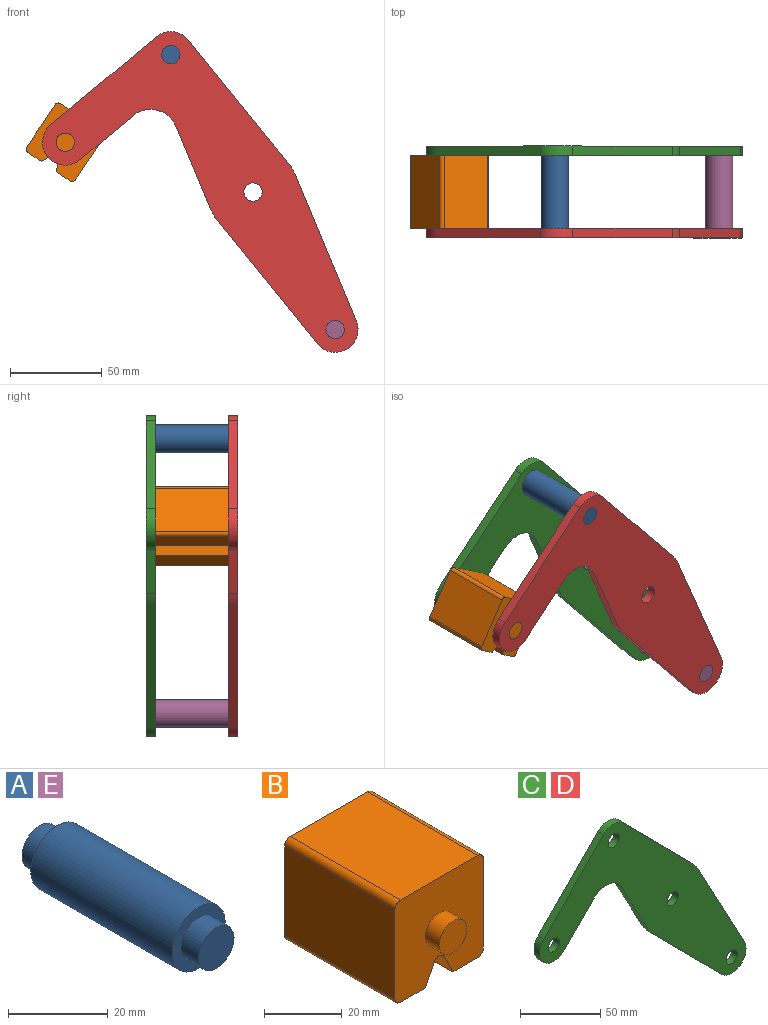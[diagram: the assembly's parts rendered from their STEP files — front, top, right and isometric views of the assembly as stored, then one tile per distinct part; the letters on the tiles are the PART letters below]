
ASSEMBLY  parts=5 mates=4
PART A: 7 faces, bbox 15x50x15 mm
  f0: cylinder r=7.5mm len=40mm, axis (0,-1,0), area 1885mm2, adj f2,f5
  f1: cylinder r=5mm len=10mm, axis (0,1,0), area 157.1mm2, adj f2,f3
  f2: plane 15x15mm, normal (0,-1,0), area 98.2mm2, adj f0,f1
  f3: plane 10x10mm, normal (0,-1,0), area 78.5mm2, adj f1
  f4: cylinder r=5mm len=10mm, axis (0,-1,0), area 157.1mm2, adj f5,f6
  f5: plane 15x15mm, normal (0,1,0), area 98.2mm2, adj f0,f4
  f6: plane 10x10mm, normal (0,1,0), area 78.5mm2, adj f4
PART B: 18 faces, bbox 32.1x50x32.1 mm
  f0: plane 40x28.08mm, normal (1,0,0), area 1123.1mm2, adj f4,f10,f13,f14
  f1: plane 40x9.04mm, normal (0,0,-1), area 361.6mm2, adj f2,f4,f10,f14
  f2: plane 40x6.42mm, normal (-0.89,0,-0.45), area 287.2mm2, adj f1,f4,f10,f15
  f3: plane 40x6.42mm, normal (0.89,0,-0.45), area 287.2mm2, adj f4,f5,f10,f15
  f4: plane 32.08x32.08mm, normal (0,-1,0), area 900.6mm2, adj f0,f1,f2,f3,f5,f6,f7,f9
  f5: plane 40x9.04mm, normal (0,0,-1), area 361.6mm2, adj f3,f4,f10,f16
  f6: plane 40x28.08mm, normal (0,0,1), area 1123.1mm2, adj f4,f10,f13,f17
  f7: plane 40x28.08mm, normal (-1,0,0), area 1123.1mm2, adj f4,f10,f16,f17
  f8: plane 10x10mm, normal (0,-1,0), area 78.5mm2, adj f9
  f9: cylinder r=5mm len=10mm, axis (0,1,0), area 157.1mm2, adj f4,f8
  f10: plane 32.08x32.08mm, normal (0,1,0), area 900.6mm2, adj f0,f1,f2,f3,f5,f6,f7,f12
  f11: plane 10x10mm, normal (0,1,0), area 78.5mm2, adj f12
  f12: cylinder r=5mm len=10mm, axis (0,-1,0), area 157.1mm2, adj f10,f11
  f13: cylinder r=2mm len=40mm, axis (0,1,0), area 125.7mm2, adj f0,f4,f6,f10
  f14: cylinder r=2mm len=40mm, axis (0,-1,0), area 125.7mm2, adj f0,f1,f4,f10
  f15: cylinder r=2mm len=40mm, axis (0,1,0), area 177.1mm2, adj f2,f3,f4,f10
  f16: cylinder r=2mm len=40mm, axis (0,1,0), area 125.7mm2, adj f4,f5,f7,f10
  f17: cylinder r=2mm len=40mm, axis (0,-1,0), area 125.7mm2, adj f4,f6,f7,f10
PART C: 18 faces, bbox 181.7x5x165.8 mm
  f0: plane 43.49x23.35mm, normal (-0.88,0,-0.47), area 246.8mm2, adj f1,f14,f16,f17
  f1: cylinder r=25mm len=5.75mm, axis (0,1,0), area 35.8mm2, adj f0,f2,f16,f17
  f2: plane 61.6x60.87mm, normal (-0.71,0,-0.7), area 433mm2, adj f1,f3,f16,f17
  f3: cylinder r=12.5mm len=21.39mm, axis (0,1,0), area 178.4mm2, adj f2,f4,f16,f17
  f4: plane 76.3x40.96mm, normal (0.88,0,0.47), area 433mm2, adj f3,f5,f16,f17
  f5: cylinder r=25mm len=5.75mm, axis (0,1,0), area 35.8mm2, adj f4,f6,f16,f17
  f6: plane 61.6x60.87mm, normal (0.71,0,0.7), area 433mm2, adj f5,f7,f16,f17
  f7: cylinder r=12.5mm len=17.78mm, axis (0,1,0), area 98.9mm2, adj f6,f8,f16,f17
  f8: plane 53.35x52.71mm, normal (-0.71,0,0.7), area 375mm2, adj f7,f9,f16,f17
  f9: cylinder r=12.5mm len=21.39mm, axis (0,1,0), area 196.3mm2, adj f8,f10,f16,f17
  f10: plane 26.86x26.54mm, normal (0.71,0,-0.7), area 188.8mm2, adj f9,f14,f16,f17
  f11: cylinder r=5mm len=10mm, axis (0,1,0), area 157.1mm2, adj f16,f17
  f12: cylinder r=5mm len=10mm, axis (0,1,0), area 157.1mm2, adj f16,f17
  f13: cylinder r=5mm len=10mm, axis (0,1,0), area 157.1mm2, adj f16,f17
  f14: cylinder r=15mm len=23.89mm, axis (0,1,0), area 140.2mm2, adj f0,f10,f16,f17
  f15: cylinder r=5mm len=10mm, axis (0,1,0), area 157.1mm2, adj f16,f17
  f16: plane 181.66x165.78mm, normal (0,-1,0), area 8710.1mm2, adj f0,f1,f2,f3,f4,f5,f6,f7
  f17: plane 181.66x165.78mm, normal (0,1,0), area 8710.1mm2, adj f0,f1,f2,f3,f4,f5,f6,f7
PART D: same geometry as C
PART E: same geometry as A
PLACE A rot(axis=(0,1,0),5.6deg) t=(0,0,0)mm
PLACE B rot(axis=(0,1,0),34.1deg) t=(-25.34,0,-45.59)mm
PLACE C rot(axis=(0,1,0),5.6deg) t=(0,45,0)mm
PLACE D rot(axis=(0,1,0),5.6deg) t=(0,0,0)mm fixed
PLACE E rot(axis=(0,1,0),5.6deg) t=(89.76,0,-150.23)mm
MATE fastened A.f0 <-> C.f7  axis (0,1,0) through (-44.88,40,75.11)mm
MATE fastened E.f0 <-> D.f3  axis (0,-1,0) through (44.88,0,-75.11)mm
MATE fastened A.f0 <-> D.f7  axis (0,-1,0) through (-44.88,0,75.11)mm
MATE revolute B.f9 <-> D.f9  axis (0,-1,0) through (-102.53,0,27.14)mm
